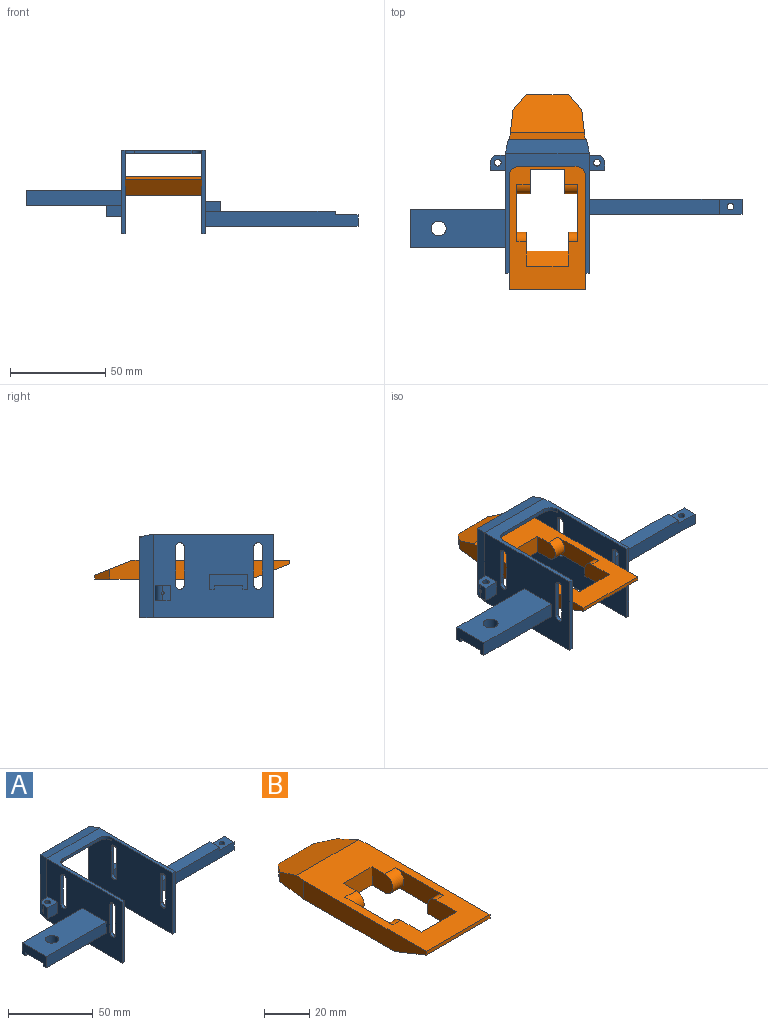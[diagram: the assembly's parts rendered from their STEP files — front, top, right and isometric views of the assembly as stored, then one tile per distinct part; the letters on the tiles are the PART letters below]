
ASSEMBLY  parts=2 mates=1
PART A: 71 faces, bbox 174x70x44 mm
  f0: cylinder r=0.75mm len=2.42mm, axis (1,0,0), area 10.9mm2, adj f66,f67,f70
  f1: plane 63x44mm, normal (-1,0,0), area 2366.2mm2, adj f6,f11,f12,f14,f18,f19,f20,f21
  f2: cylinder r=0.75mm len=2.42mm, axis (-1,0,0), area 10.9mm2, adj f57,f58,f61
  f3: plane 63x44mm, normal (1,0,0), area 2432.2mm2, adj f8,f9,f12,f16,f17,f22,f23,f24
  f4: plane 70x44mm, normal (-1,0,0), area 2830.2mm2, adj f12,f13,f15,f16,f17,f22,f23,f24
  f5: plane 70x44mm, normal (1,0,0), area 2830.2mm2, adj f11,f12,f13,f14,f15,f18,f19,f20
  f6: plane 50x2.5mm, normal (0,0,-1), area 125mm2, adj f1,f7,f35,f38
  f7: plane 20x8mm, normal (-1,0,0), area 130mm2, adj f6,f33,f34,f35,f36,f37,f38,f39
  f8: plane 68x8mm, normal (0,0,1), area 544mm2, adj f3,f9,f29,f32
  f9: plane 80x8mm, normal (0,-1,0), area 616mm2, adj f3,f8,f10,f30,f31,f32
  f10: plane 8x6mm, normal (1,0,0), area 48mm2, adj f9,f29,f30,f31
  f11: plane 44x2mm, normal (0,-1,0), area 88mm2, adj f1,f5,f12,f14
  f12: plane 63x44mm, normal (0,0,1), area 542.7mm2, adj f1,f3,f4,f5,f11,f17,f26,f27
  f13: plane 40x19mm, normal (0,0,-1), area 570.7mm2, adj f4,f5,f15,f26,f27,f28
  f14: plane 70x2mm, normal (0,0,-1), area 134.8mm2, adj f1,f5,f11,f15,f43
  f15: plane 42.5x41mm, normal (0,1,0), area 62.5mm2, adj f4,f5,f13,f14,f16,f41,f42,f43
  f16: plane 70x2mm, normal (0,0,-1), area 134.8mm2, adj f3,f4,f15,f17,f41
  f17: plane 44x2mm, normal (0,-1,0), area 88mm2, adj f3,f4,f12,f16
  f18: cylinder r=2.25mm len=4.5mm, axis (1,0,0), area 14.1mm2, adj f1,f5,f19,f21
  f19: plane 20x2mm, normal (0,1,0), area 40mm2, adj f1,f5,f18,f20
  f20: cylinder r=2.25mm len=4.5mm, axis (1,0,0), area 14.1mm2, adj f1,f5,f19,f21
  f21: plane 20x2mm, normal (0,-1,0), area 40mm2, adj f1,f5,f18,f20
  f22: plane 20x2mm, normal (0,-1,0), area 40mm2, adj f3,f4,f23,f25
  f23: cylinder r=2.25mm len=4.5mm, axis (1,0,0), area 14.1mm2, adj f3,f4,f22,f24
  f24: plane 20x2mm, normal (0,1,0), area 40mm2, adj f3,f4,f23,f25
  f25: cylinder r=2.25mm len=4.5mm, axis (1,0,0), area 14.1mm2, adj f3,f4,f22,f24
  f26: cylinder r=5mm len=5mm, axis (0,0,1), area 15.7mm2, adj f4,f12,f13,f27
  f27: plane 30x2mm, normal (0,-1,0), area 60mm2, adj f12,f13,f26,f28
  f28: cylinder r=5mm len=5mm, axis (0,0,1), area 15.7mm2, adj f5,f12,f13,f27
  f29: plane 80x8mm, normal (0,1,0), area 616mm2, adj f3,f8,f10,f30,f31,f32
  f30: plane 80x8mm, normal (0,0,-1), area 630.4mm2, adj f3,f9,f10,f29,f44
  f31: plane 12x8mm, normal (0,0,1), area 86.4mm2, adj f9,f10,f29,f32,f44
  f32: plane 8x2mm, normal (1,0,0), area 16mm2, adj f8,f9,f29,f31
  f33: plane 50x8mm, normal (0,1,0), area 400mm2, adj f1,f7,f34,f36
  f34: plane 50x2.5mm, normal (0,0,-1), area 125mm2, adj f1,f7,f33,f37
  f35: plane 50x8mm, normal (0,-1,0), area 400mm2, adj f1,f6,f7,f36
  f36: plane 50x20mm, normal (0,0,1), area 952.2mm2, adj f1,f7,f33,f35,f40
  f37: plane 50x2mm, normal (0,-1,0), area 100mm2, adj f1,f7,f34,f39
  f38: plane 50x2mm, normal (0,1,0), area 100mm2, adj f1,f6,f7,f39
  f39: plane 50x15mm, normal (0,0,-1), area 702.2mm2, adj f1,f7,f37,f38,f40
  f40: cylinder r=3.9mm len=7.8mm, axis (0,0,1), area 147mm2, adj f36,f39
  f41: plane 44x7mm, normal (0.98,0.21,0), area 309.6mm2, adj f3,f15,f16,f42
  f42: plane 44x7mm, normal (0,0.21,0.98), area 304.3mm2, adj f12,f15,f41,f43
  f43: plane 44x7mm, normal (-0.98,0.21,0), area 309.6mm2, adj f1,f14,f15,f42
  f44: cylinder r=1.75mm len=6mm, axis (0,0,1), area 66mm2, adj f30,f31
  f45: cylinder r=2.25mm len=4.5mm, axis (1,0,0), area 14.1mm2, adj f1,f5,f46,f48
  f46: plane 20x2mm, normal (0,1,0), area 40mm2, adj f1,f5,f45,f47
  f47: cylinder r=2.25mm len=4.5mm, axis (1,0,0), area 14.1mm2, adj f1,f5,f46,f48
  f48: plane 20x2mm, normal (0,-1,0), area 40mm2, adj f1,f5,f45,f47
  f49: plane 20x2mm, normal (0,-1,0), area 40mm2, adj f3,f4,f50,f52
  f50: cylinder r=2.25mm len=4.5mm, axis (1,0,0), area 14.1mm2, adj f3,f4,f49,f51
  f51: plane 20x2mm, normal (0,1,0), area 40mm2, adj f3,f4,f50,f52
  f52: cylinder r=2.25mm len=4.5mm, axis (1,0,0), area 14.1mm2, adj f3,f4,f49,f51
  f53: plane 8x4mm, normal (0,1,0), area 32mm2, adj f3,f54,f56,f61
  f54: plane 8x8mm, normal (0,0,1), area 50.9mm2, adj f3,f53,f55,f57,f58,f61
  f55: plane 8x8mm, normal (0,-1,0), area 64mm2, adj f3,f54,f56,f57
  f56: plane 8x8mm, normal (0,0,-1), area 50.9mm2, adj f3,f53,f55,f57,f58,f61
  f57: plane 8x4mm, normal (1,0,0), area 31.1mm2, adj f2,f54,f55,f56,f61
  f58: cylinder r=1.75mm len=8mm, axis (0,0,1), area 84.3mm2, adj f2,f54,f56,f60
  f59: plane 1.5x1.5mm, normal (1,0,0), area 1.8mm2, adj f60
  f60: cylinder r=0.75mm len=2.42mm, axis (-1,0,0), area 11mm2, adj f58,f59
  f61: cylinder r=4mm len=8mm, axis (0,0,-1), area 49.4mm2, adj f2,f53,f54,f56,f57
  f62: plane 8x8mm, normal (0,-1,0), area 64mm2, adj f1,f63,f65,f66
  f63: plane 8x8mm, normal (0,0,1), area 50.9mm2, adj f1,f62,f64,f66,f67,f70
  f64: plane 8x4mm, normal (0,1,0), area 32mm2, adj f1,f63,f65,f70
  f65: plane 8x8mm, normal (0,0,-1), area 50.9mm2, adj f1,f62,f64,f66,f67,f70
  f66: plane 8x4mm, normal (-1,0,0), area 31.1mm2, adj f0,f62,f63,f65,f70
  f67: cylinder r=1.75mm len=8mm, axis (0,0,1), area 84.3mm2, adj f0,f63,f65,f69
  f68: plane 1.5x1.5mm, normal (-1,0,0), area 1.8mm2, adj f69
  f69: cylinder r=0.75mm len=2.42mm, axis (1,0,0), area 11mm2, adj f67,f68
  f70: cylinder r=4mm len=8mm, axis (0,0,1), area 49.4mm2, adj f0,f63,f64,f65,f66
PART B: 26 faces, bbox 40x102x10 mm
  f0: plane 77x10mm, normal (-1,0,0), area 690mm2, adj f1,f4,f5,f6,f9
  f1: plane 40x2mm, normal (0,-1,0), area 80mm2, adj f0,f2,f4,f6
  f2: plane 77x10mm, normal (1,0,0), area 690mm2, adj f1,f4,f5,f6,f8
  f3: plane 22x2mm, normal (0,1,0), area 44mm2, adj f5,f7,f10,f11
  f4: plane 82x40mm, normal (0,0,1), area 1887mm2, adj f0,f1,f2,f7,f8,f9,f12,f13
  f5: plane 82x40mm, normal (0,0,-1), area 1993.3mm2, adj f0,f2,f3,f6,f8,f9,f10,f11
  f6: plane 40x20mm, normal (0,-0.37,-0.93), area 861.6mm2, adj f0,f1,f2,f5,f23
  f7: plane 38.8x20mm, normal (0,0.37,0.93), area 732.8mm2, adj f3,f4,f8,f9,f10,f11
  f8: plane 17.06x10mm, normal (0.99,0.12,0), area 142.5mm2, adj f2,f4,f5,f7,f10
  f9: plane 17.06x10mm, normal (-0.99,0.12,0), area 142.5mm2, adj f0,f4,f5,f7,f11
  f10: plane 7.94x6.95mm, normal (0.75,0.66,0), area 37.9mm2, adj f3,f5,f7,f8
  f11: plane 7.94x6.95mm, normal (-0.75,0.66,0), area 37.9mm2, adj f3,f5,f7,f9
  f12: plane 18x10mm, normal (1,0,0), area 134.6mm2, adj f4,f5,f20,f23,f25
  f13: plane 18x10mm, normal (-1,0,0), area 134.6mm2, adj f4,f5,f14,f23,f24
  f14: plane 5x5mm, normal (0,1,0), area 25mm2, adj f5,f13,f15,f24
  f15: plane 30x10mm, normal (-1,0,0), area 216.1mm2, adj f4,f5,f14,f22,f24
  f16: plane 13x10mm, normal (-1,0,0), area 119.3mm2, adj f4,f5,f17,f22
  f17: plane 18x10mm, normal (0,-1,0), area 180mm2, adj f4,f5,f16,f18
  f18: plane 13x10mm, normal (1,0,0), area 119.3mm2, adj f4,f5,f17,f21
  f19: plane 30x10mm, normal (1,0,0), area 216.1mm2, adj f4,f5,f20,f21,f25
  f20: plane 5x5mm, normal (0,1,0), area 25mm2, adj f5,f12,f19,f25
  f21: cylinder r=5mm len=10mm, axis (-1,0,0), area 110mm2, adj f4,f5,f18,f19
  f22: cylinder r=5mm len=10mm, axis (-1,0,0), area 110mm2, adj f4,f5,f15,f16
  f23: plane 22x10mm, normal (0,0.78,0.62), area 281.7mm2, adj f4,f6,f12,f13
  f24: cylinder r=5mm len=5mm, axis (-1,0,0), area 39.3mm2, adj f4,f13,f14,f15
  f25: cylinder r=5mm len=5mm, axis (-1,0,0), area 39.3mm2, adj f4,f12,f19,f20
PLACE A t=(-53.82,-12.96,-0.97)mm
PLACE B t=(-31.82,29.69,19.38)mm
MATE planar A.f5 <-> B.f0  axis (1,0,0) through (-51.82,22.19,20.35)mm
